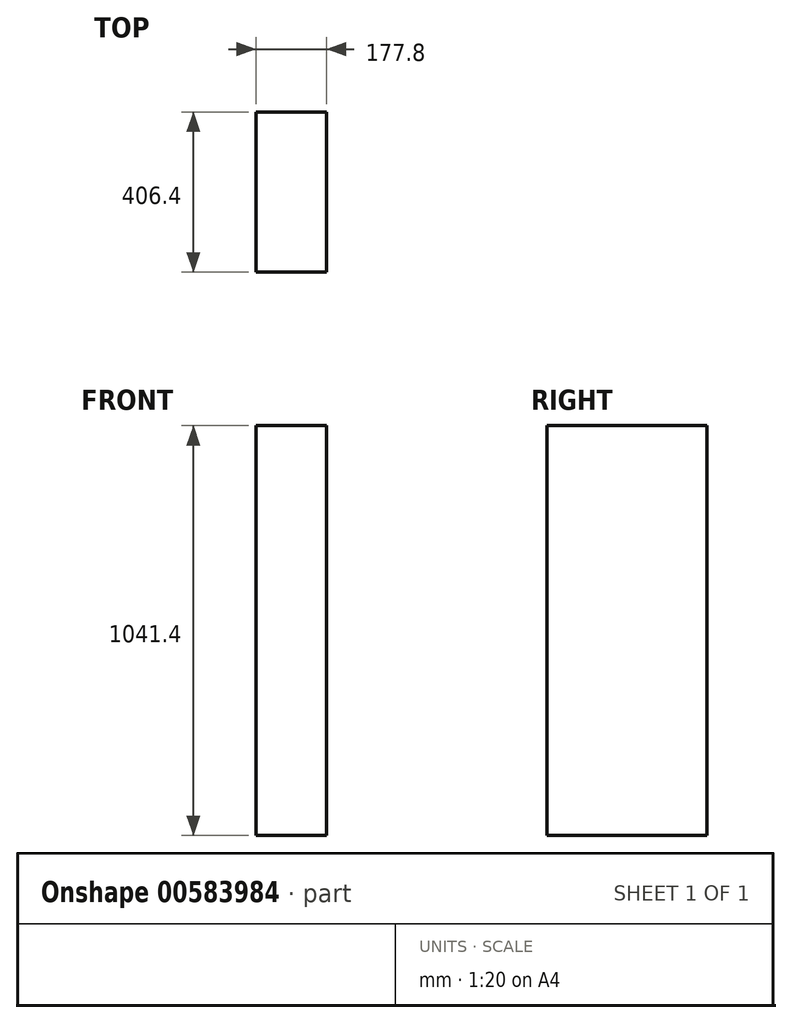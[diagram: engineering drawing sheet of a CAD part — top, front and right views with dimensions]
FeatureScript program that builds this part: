
annotation { "Feature Type Name" : "Feature", "Feature Type Description" : "" }
export const myFeature = defineFeature(function(context is Context, id is Id, definition is map)
    precondition{}
    {
        {
            var Q0;
            Q0=qCreatedBy(makeId("Top.planeOp"),FACE);
            var sketch = newSketch(context, id + "F0", { "sketchPlane" : qUnion([Q0])});
            skLineSegment(sketch, "E0.bottom", {"start": v(-86.9, 349.54) * mm, "end": v(90.9, 349.54) * mm});
            skLineSegment(sketch, "E0.top", {"start": v(-86.9, -56.86) * mm, "end": v(90.9, -56.86) * mm});
            skLineSegment(sketch, "E0.left", {"start": v(-86.9, 349.54) * mm, "end": v(-86.9, -56.86) * mm});
            skLineSegment(sketch, "E0.right", {"start": v(90.9, 349.54) * mm, "end": v(90.9, -56.86) * mm});
            skSolve(sketch);
        }
        {
            var Q0;
            Q0=makeQuery(id+"F0.imprint","IMPRINT",FACE,{"disambiguationData":[TD([[makeQuery(id+"F0.imprint","IMPRINT",EDGE,{"derivedFrom":sQuery(id+"F0.wireOp",EDGE,"E0.bottom")}),-1.0]])]});
            extrude(context, id + "F1", {"entities" : qUnion([Q0]), "depth" : 1041.4 * mm, "offsetDistance" : 25.4 * mm});
        }
    });
